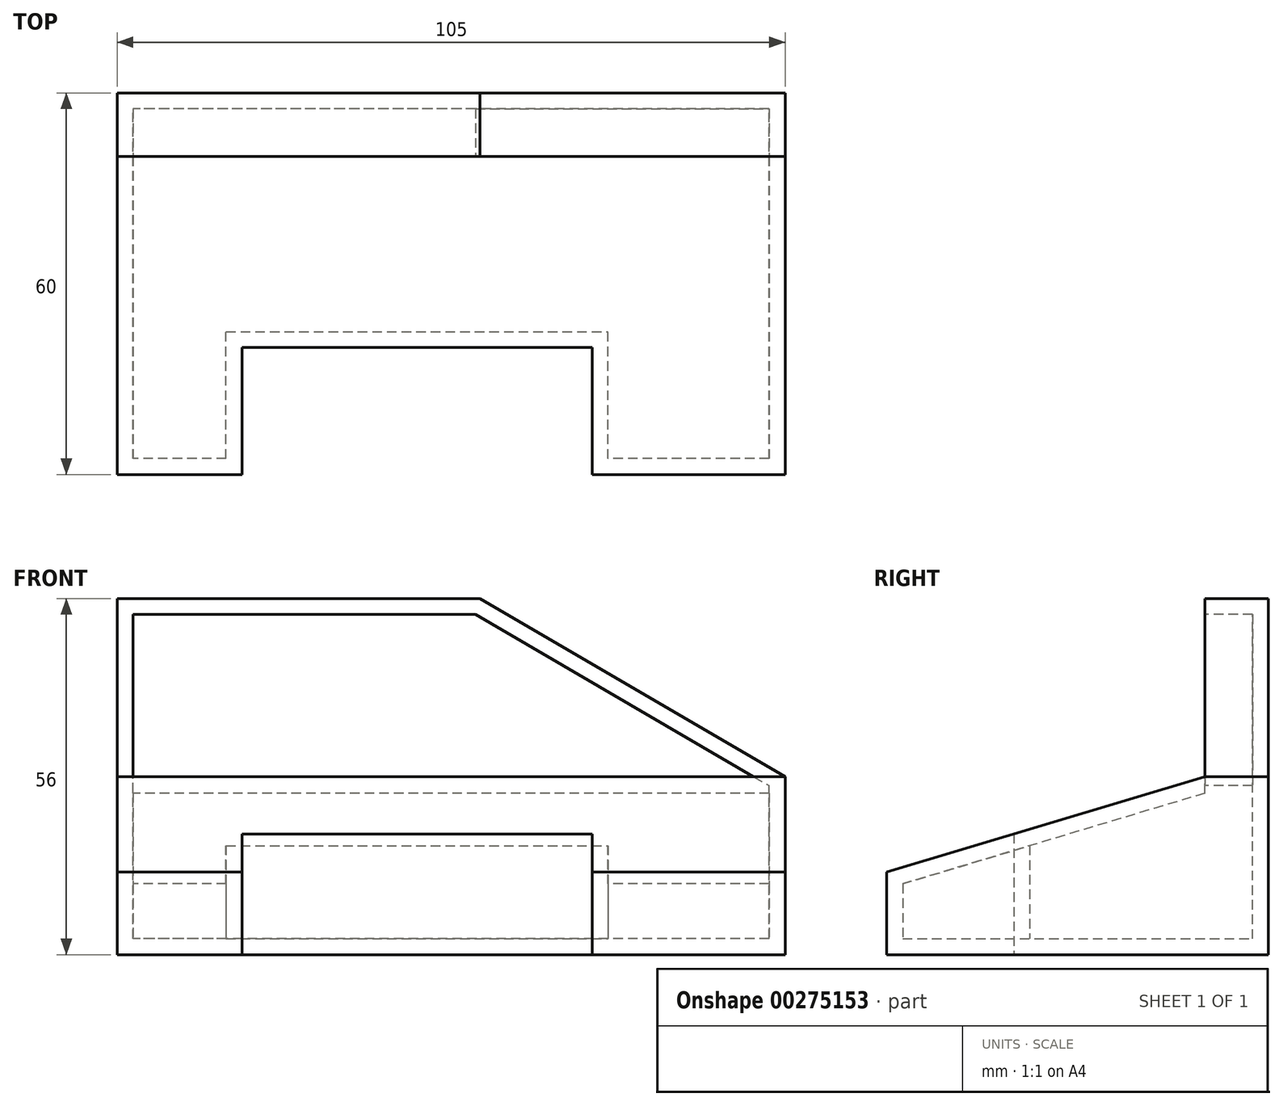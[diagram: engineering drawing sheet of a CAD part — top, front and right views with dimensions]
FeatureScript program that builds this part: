
annotation { "Feature Type Name" : "Feature", "Feature Type Description" : "" }
export const myFeature = defineFeature(function(context is Context, id is Id, definition is map)
    precondition{}
    {
        {
            var Q0;
            Q0=qCreatedBy(makeId("Right.planeOp"),FACE);
            var sketch = newSketch(context, id + "F0", { "sketchPlane" : qUnion([Q0])});
            skLineSegment(sketch, "E0", {"start": v(0, 0) * mm, "end": v(0, 56) * mm});
            skLineSegment(sketch, "E1", {"start": v(0, 56) * mm, "end": v(-10, 56) * mm});
            skLineSegment(sketch, "E2", {"start": v(-10, 28) * mm, "end": v(-60, 13) * mm});
            skLineSegment(sketch, "E3", {"start": v(-60, 13) * mm, "end": v(-60, 0) * mm});
            skLineSegment(sketch, "E4", {"start": v(-60, 0) * mm, "end": v(0, 0) * mm});
            skLineSegment(sketch, "E5", {"start": v(-10, 28) * mm, "end": v(-10, 56) * mm});
            skSolve(sketch);
        }
        {
            var Q0;
            Q0 = qSketchRegion(id + "F0", true);
            extrude(context, id + "F1", {"entities" : qUnion([Q0]), "depth" : 105 * mm});
        }
        {
            var Q0;
            Q0=makeQuery(id+"F1.opExtrude","SWEPT_FACE",FACE,{"disambiguationData":[OSD([sQuery(id+"F0.wireOp",EDGE,"E5")])]});
            var sketch = newSketch(context, id + "F2", { "sketchPlane" : qUnion([Q0])});
            skLineSegment(sketch, "E6", {"start": v(57, 56) * mm, "end": v(105, 28) * mm});
            skSolve(sketch);
        }
        {
            var Q0;
            {var subQ0=sQuery(id+"F2.wireOp",EDGE,"E6");Q0=makeQuery(id+"F2.imprint","IMPRINT",FACE,{"disambiguationData":[TD([[makeQuery(id+"F2.imprint","IMPRINT",EDGE,{"derivedFrom":subQ0}),1.0]])]});}
            var Q1;
            Q1=makeQuery(id+"F1.opExtrude","SWEPT_FACE",FACE,{"disambiguationData":[OSD([sQuery(id+"F0.wireOp",EDGE,"E0")])]});
            extrude(context, id + "F3", {"entities" : qUnion([Q0]), "operationType" : NewBodyOperationType.REMOVE, "endBound" : BoundingType.THROUGH_ALL, "oppositeDirection" : true, "endBoundEntityFace" : qUnion([Q1]), "depth" : 25 * mm});
        }
        {
            var Q0;
            Q0=makeQuery(id+"F1.opExtrude","SWEPT_FACE",FACE,{"disambiguationData":[OSD([sQuery(id+"F0.wireOp",EDGE,"E4")])]});
            var sketch = newSketch(context, id + "F4", { "sketchPlane" : qUnion([Q0])});
            skLineSegment(sketch, "E7.bottom", {"start": v(19.61, 60) * mm, "end": v(74.66, 60) * mm});
            skLineSegment(sketch, "E7.top", {"start": v(19.61, 40.03) * mm, "end": v(74.66, 40.03) * mm});
            skLineSegment(sketch, "E7.left", {"start": v(19.61, 60) * mm, "end": v(19.61, 40.03) * mm});
            skLineSegment(sketch, "E7.right", {"start": v(74.66, 60) * mm, "end": v(74.66, 40.03) * mm});
            skSolve(sketch);
        }
        {
            var Q0;
            Q0 = qSketchRegion(id + "F4", true);
            extrude(context, id + "F5", {"entities" : qUnion([Q0]), "operationType" : NewBodyOperationType.REMOVE, "endBound" : BoundingType.THROUGH_ALL, "oppositeDirection" : true, "depth" : 75 * mm});
        }
        {
            var Q0;
            Q0=makeQuery(id+"F1.opExtrude","SWEPT_FACE",FACE,{"disambiguationData":[OSD([sQuery(id+"F0.wireOp",EDGE,"E5")])]});
            shell(context, id + "F6", {"entities" : qUnion([Q0]), "thickness" : 2.5 * mm});
        }
    });
